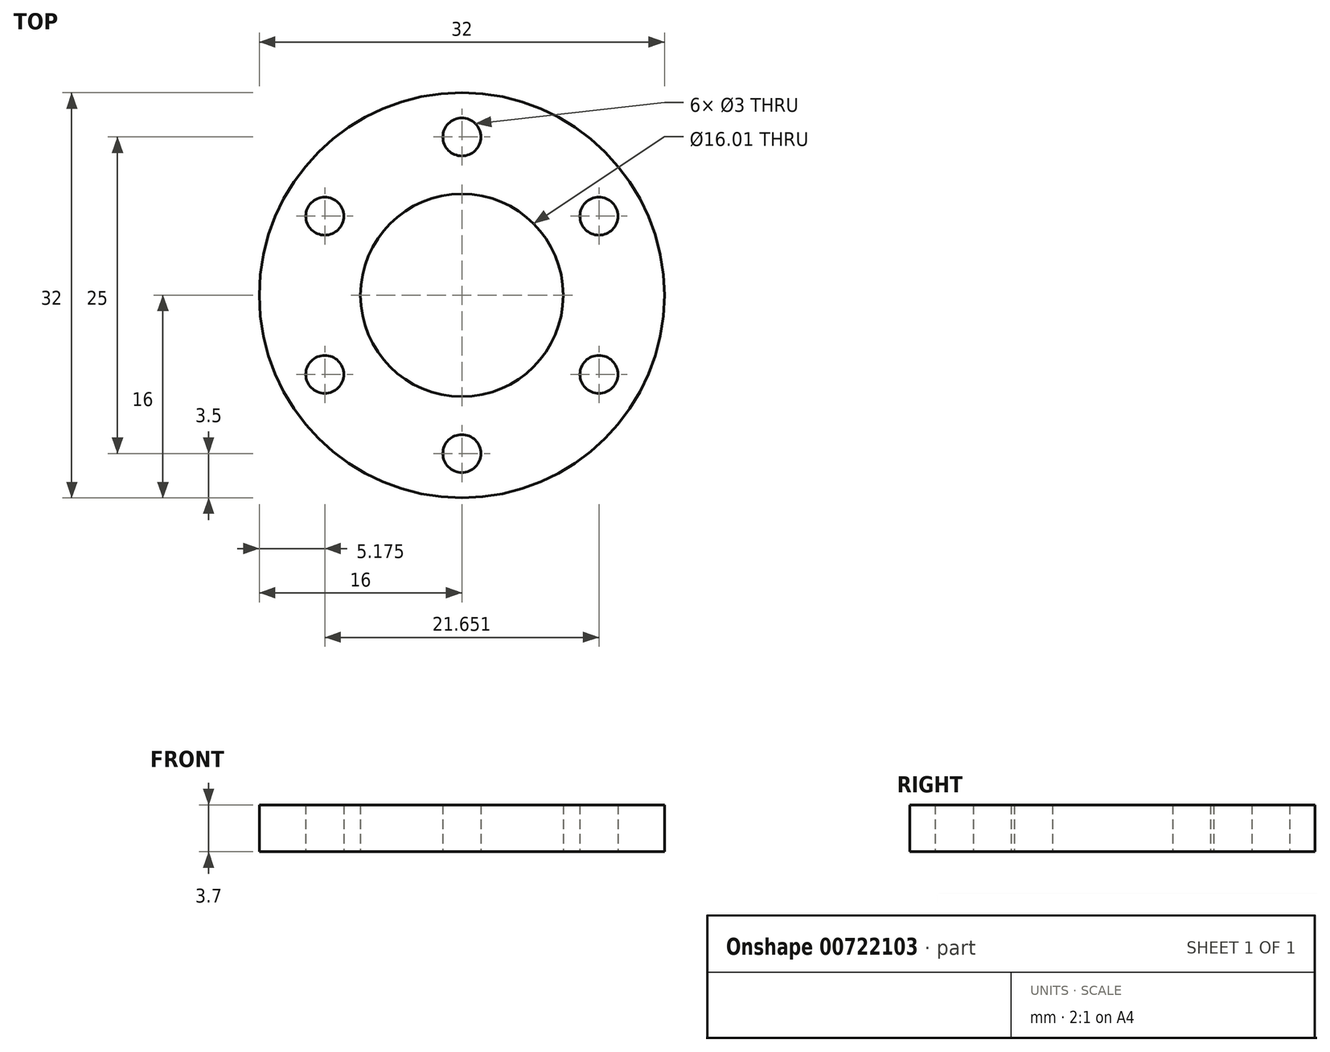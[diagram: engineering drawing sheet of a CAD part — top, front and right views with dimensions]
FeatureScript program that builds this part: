
annotation { "Feature Type Name" : "Feature", "Feature Type Description" : "" }
export const myFeature = defineFeature(function(context is Context, id is Id, definition is map)
    precondition{}
    {
        {
            var Q0;
            Q0=qCreatedBy(makeId("Top.planeOp"),FACE);
            var sketch = newSketch(context, id + "F0", { "sketchPlane" : qUnion([Q0])});
            skCircle(sketch, "E0", {"center": v(0, 0) * mm, "radius": 8 * mm});
            skCircle(sketch, "E1", {"center": v(0, 0) * mm, "radius": 16 * mm});
            skCircle(sketch, "E2", {"center": v(0, -12.5) * mm, "radius": 1.5 * mm});
            skCircle(sketch, "E3.1.0", {"center": v(10.83, -6.25) * mm, "radius": 1.5 * mm});
            skCircle(sketch, "E3.2.0", {"center": v(10.83, 6.25) * mm, "radius": 1.5 * mm});
            skCircle(sketch, "E3.3.0", {"center": v(0, 12.5) * mm, "radius": 1.5 * mm});
            skCircle(sketch, "E3.4.0", {"center": v(-10.83, 6.25) * mm, "radius": 1.5 * mm});
            skCircle(sketch, "E3.5.0", {"center": v(-10.83, -6.25) * mm, "radius": 1.5 * mm});
            skSolve(sketch);
        }
        {
            var Q0;
            Q0 = qSketchRegion(id + "F0", true);
            extrude(context, id + "F1", {"entities" : qUnion([Q0]), "depth" : 3.7 * mm, "offsetDistance" : 25 * mm});
        }
    });
